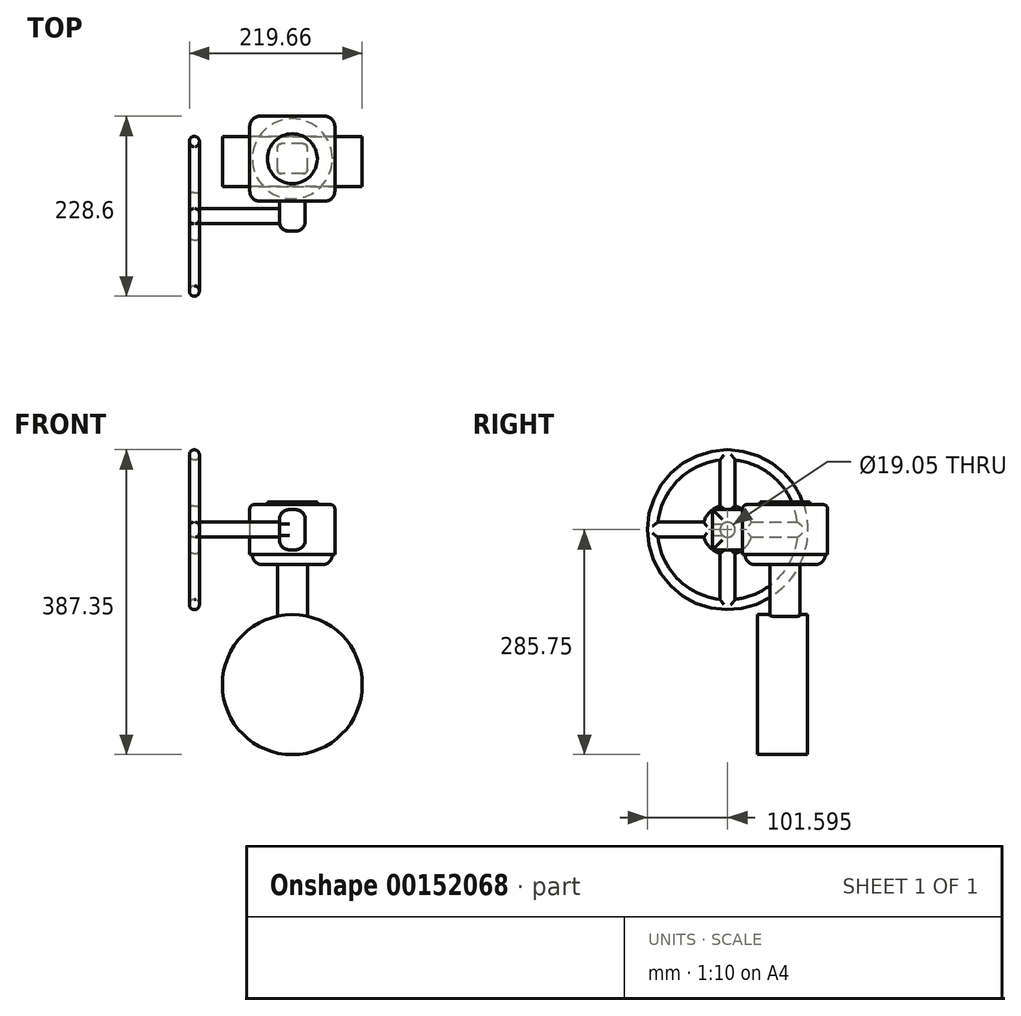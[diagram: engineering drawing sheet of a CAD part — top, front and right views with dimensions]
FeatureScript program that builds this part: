
annotation { "Feature Type Name" : "Feature", "Feature Type Description" : "" }
export const myFeature = defineFeature(function(context is Context, id is Id, definition is map)
    precondition{}
    {
        {
            var Q0;
            Q0=qCreatedBy(makeId("Front.planeOp"),FACE);
            var sketch = newSketch(context, id + "F0", { "sketchPlane" : qUnion([Q0])});
            skCircle(sketch, "E0", {"center": v(0, 0) * mm, "radius": 88.9 * mm});
            skSolve(sketch);
        }
        {
            var Q0;
            Q0=qSketchRegion(id+"F0",true);
            extrude(context, id + "F1", {"entities" : qUnion([Q0]), "depth" : 63.5 * mm});
        }
        {
            var Q0;
            Q0=qCreatedBy(makeId("Top.planeOp"),FACE);
            var sketch = newSketch(context, id + "F2", { "sketchPlane" : qUnion([Q0])});
            skLineSegment(sketch, "E1.bottom", {"start": v(19.05, -9.05) * mm, "end": v(-19.05, -9.05) * mm});
            skLineSegment(sketch, "E1.top", {"start": v(19.05, -47.15) * mm, "end": v(-19.05, -47.15) * mm});
            skLineSegment(sketch, "E1.left", {"start": v(19.05, -9.05) * mm, "end": v(19.05, -47.15) * mm});
            skLineSegment(sketch, "E1.right", {"start": v(-19.05, -9.05) * mm, "end": v(-19.05, -47.15) * mm});
            skPoint(sketch, "E1.middle", {"position": v(0, -28.1) * mm});
            skSolve(sketch);
        }
        {
            var Q0;
            Q0=qSketchRegion(id+"F2",true);
            extrude(context, id + "F3", {"entities" : qUnion([Q0]), "operationType" : NewBodyOperationType.ADD, "depth" : 152.4 * mm});
        }
        {
            var Q0;
            Q0=makeQuery(id+"F3.opExtrude","CAP_FACE",FACE,{"disambiguationData":[OSD([sQuery(id+"F2.wireOp",EDGE,"E1.bottom"),sQuery(id+"F2.wireOp",EDGE,"E1.top"),sQuery(id+"F2.wireOp",EDGE,"E1.left"),sQuery(id+"F2.wireOp",EDGE,"E1.right")])],"isStart":false});
            var sketch = newSketch(context, id + "F4", { "sketchPlane" : qUnion([Q0])});
            skCircle(sketch, "E2", {"center": v(0, -28.1) * mm, "radius": 50.8 * mm});
            skPoint(sketch, "E2.centerSnap0", {"position": v(19.05, -28.1) * mm});
            skSolve(sketch);
        }
        {
            var Q0;
            Q0=qSketchRegion(id+"F4",true);
            extrude(context, id + "F5", {"entities" : qUnion([Q0]), "operationType" : NewBodyOperationType.ADD, "depth" : 12.7 * mm});
        }
        {
            var Q0;
            Q0=makeQuery(id+"F5.opExtrude","CAP_FACE",FACE,{"disambiguationData":[OSD([sQuery(id+"F4.wireOp",EDGE,"E2")])],"isStart":false});
            var sketch = newSketch(context, id + "F6", { "sketchPlane" : qUnion([Q0])});
            skCircle(sketch, "E3", {"center": v(0, -28.1) * mm, "radius": 9.5 * mm});
            skSolve(sketch);
        }
        {
            var Q0;
            Q0=makeQuery(id+"F3.opExtrude","SWEPT_EDGE",EDGE,{"disambiguationData":[OSD([sQuery(id+"F2.wireOp",EDGE,"E1.top"),sQuery(id+"F2.wireOp",EDGE,"E1.right")])]});
            var Q1;
            Q1=makeQuery(id+"F3.opExtrude","SWEPT_EDGE",EDGE,{"disambiguationData":[OSD([sQuery(id+"F2.wireOp",EDGE,"E1.top"),sQuery(id+"F2.wireOp",EDGE,"E1.left")])]});
            var Q2;
            Q2=makeQuery(id+"F3.opExtrude","SWEPT_EDGE",EDGE,{"disambiguationData":[OSD([sQuery(id+"F2.wireOp",EDGE,"E1.bottom"),sQuery(id+"F2.wireOp",EDGE,"E1.left")])]});
            var Q3;
            Q3=makeQuery(id+"F3.opExtrude","SWEPT_EDGE",EDGE,{"disambiguationData":[OSD([sQuery(id+"F2.wireOp",EDGE,"E1.bottom"),sQuery(id+"F2.wireOp",EDGE,"E1.right")])]});
            fillet(context, id + "F7", {"entities" : qUnion([Q0, Q1, Q2, Q3]), "radius" : 5.08 * mm, "tangentPropagation" : true, "allowEdgeOverflow" : false});
        }
        {
            var Q0;
            Q0=sQuery(id+"F6.wireOp",EDGE,"E3");
            extrude(context, id + "F8", {"bodyType" : ToolBodyType.SURFACE, "surfaceEntities" : qUnion([Q0]), "depth" : 31.75 * mm});
        }
        {
            var Q0;
            Q0=makeQuery(id+"F5.opExtrude","CAP_FACE",FACE,{"disambiguationData":[OSD([sQuery(id+"F4.wireOp",EDGE,"E2")])],"isStart":false});
            var sketch = newSketch(context, id + "F9", { "sketchPlane" : qUnion([Q0])});
            skLineSegment(sketch, "E4.bottom", {"start": v(53.98, 25.88) * mm, "end": v(-53.98, 25.88) * mm});
            skLineSegment(sketch, "E4.top", {"start": v(53.97, -82.07) * mm, "end": v(-53.98, -82.07) * mm});
            skLineSegment(sketch, "E4.left", {"start": v(53.98, 25.88) * mm, "end": v(53.97, -82.07) * mm});
            skLineSegment(sketch, "E4.right", {"start": v(-53.97, 25.88) * mm, "end": v(-53.98, -82.07) * mm});
            skPoint(sketch, "E4.middle", {"position": v(0, -28.1) * mm});
            skSolve(sketch);
        }
        {
            var Q0;
            Q0 = qSketchRegion(id + "F9", true);
            extrude(context, id + "F10", {"entities" : qUnion([Q0]), "operationType" : NewBodyOperationType.ADD, "depth" : 63.5 * mm});
        }
        {
            var Q0;
            Q0=makeQuery(id+"F10.opExtrude","SWEPT_FACE",FACE,{"disambiguationData":[OSD([sQuery(id+"F9.wireOp",EDGE,"E4.top")])]});
            var sketch = newSketch(context, id + "F11", { "sketchPlane" : qUnion([Q0])});
            skLineSegment(sketch, "E5.bottom", {"start": v(16.46, 222.43) * mm, "end": v(-16.46, 222.43) * mm});
            skLineSegment(sketch, "E5.top", {"start": v(16.46, 171.27) * mm, "end": v(-16.46, 171.27) * mm});
            skLineSegment(sketch, "E5.left", {"start": v(16.46, 222.43) * mm, "end": v(16.46, 171.27) * mm});
            skLineSegment(sketch, "E5.right", {"start": v(-16.46, 222.43) * mm, "end": v(-16.46, 171.27) * mm});
            skPoint(sketch, "E5.middle", {"position": v(0, 196.85) * mm});
            skPoint(sketch, "E5.middle.positionSnap0", {"position": v(53.98, 196.85) * mm});
            skPoint(sketch, "E5.centerSnap0", {"position": v(53.98, 196.85) * mm});
            skSolve(sketch);
        }
        {
            var Q0;
            Q0 = qSketchRegion(id + "F11", true);
            extrude(context, id + "F12", {"entities" : qUnion([Q0]), "operationType" : NewBodyOperationType.ADD, "depth" : 38.1 * mm});
        }
        {
            var Q0;
            Q0=makeQuery(id+"F12.opExtrude","SWEPT_FACE",FACE,{"disambiguationData":[OSD([sQuery(id+"F11.wireOp",EDGE,"E5.right")])]});
            var sketch = newSketch(context, id + "F13", { "sketchPlane" : qUnion([Q0])});
            skCircle(sketch, "E6", {"center": v(101.12, 196.85) * mm, "radius": 9.53 * mm});
            skPoint(sketch, "E6.centerSnap0", {"position": v(101.12, 171.27) * mm});
            skPoint(sketch, "E6.centerSnap1", {"position": v(120.17, 196.85) * mm});
            skSolve(sketch);
        }
        {
            var Q0;
            Q0 = qSketchRegion(id + "F13", true);
            extrude(context, id + "F14", {"entities" : qUnion([Q0]), "operationType" : NewBodyOperationType.ADD, "depth" : 101.6 * mm});
        }
        {
            var Q0;
            Q0=makeQuery(id+"F14.opExtrude","CAP_FACE",FACE,{"disambiguationData":[OSD([sQuery(id+"F13.wireOp",EDGE,"E6")])],"isStart":false});
            var sketch = newSketch(context, id + "F15", { "sketchPlane" : qUnion([Q0])});
            skCircle(sketch, "E7", {"center": v(101.12, 196.85) * mm, "radius": 101.6 * mm});
            skCircle(sketch, "E8", {"center": v(101.12, 196.85) * mm, "radius": 31.75 * mm});
            skCircle(sketch, "E9", {"center": v(101.12, 196.85) * mm, "radius": 88.9 * mm});
            skLineSegment(sketch, "E10.bottom", {"start": v(189.51, 206.37) * mm, "end": v(131.41, 206.37) * mm});
            skLineSegment(sketch, "E10.top", {"start": v(189.51, 187.32) * mm, "end": v(131.41, 187.32) * mm});
            skPoint(sketch, "E10.middle", {"position": v(158.95, 196.85) * mm});
            skLineSegment(sketch, "E11.left", {"start": v(110.65, 166.56) * mm, "end": v(110.65, 108.46) * mm});
            skLineSegment(sketch, "E11.right", {"start": v(91.6, 166.56) * mm, "end": v(91.6, 108.46) * mm});
            skPoint(sketch, "E11.middle", {"position": v(101.12, 139.25) * mm});
            skLineSegment(sketch, "E12.bottom", {"start": v(70.84, 206.38) * mm, "end": v(12.74, 206.38) * mm});
            skLineSegment(sketch, "E12.top", {"start": v(70.84, 187.32) * mm, "end": v(12.74, 187.32) * mm});
            skPoint(sketch, "E12.middle", {"position": v(45.52, 196.85) * mm});
            skLineSegment(sketch, "E13.left", {"start": v(110.65, 285.24) * mm, "end": v(110.65, 227.14) * mm});
            skLineSegment(sketch, "E13.right", {"start": v(91.6, 285.24) * mm, "end": v(91.6, 227.14) * mm});
            skPoint(sketch, "E13.middle", {"position": v(101.12, 255.79) * mm});
            skPoint(sketch, "E14.orphan", {"position": v(110.65, 102.77) * mm});
            skPoint(sketch, "E15.orphan", {"position": v(91.6, 102.77) * mm});
            skPoint(sketch, "E16.orphan", {"position": v(110.65, 175.72) * mm});
            skPoint(sketch, "E17.orphan", {"position": v(91.6, 175.72) * mm});
            skPoint(sketch, "E18.orphan", {"position": v(127.2, 206.37) * mm});
            skPoint(sketch, "E19.orphan", {"position": v(127.2, 187.32) * mm});
            skPoint(sketch, "E20.orphan", {"position": v(190.7, 187.32) * mm});
            skPoint(sketch, "E21.orphan", {"position": v(190.7, 206.37) * mm});
            skPoint(sketch, "E22.orphan", {"position": v(91.6, 217.69) * mm});
            skPoint(sketch, "E13.top.start.orphan", {"position": v(110.65, 217.69) * mm});
            skPoint(sketch, "E23.orphan", {"position": v(91.6, 293.89) * mm});
            skPoint(sketch, "E13.bottom.start.orphan", {"position": v(110.65, 293.89) * mm});
            skPoint(sketch, "E24.orphan", {"position": v(83.62, 206.38) * mm});
            skPoint(sketch, "E12.left.end.orphan", {"position": v(83.62, 187.32) * mm});
            skPoint(sketch, "E25.orphan", {"position": v(7.42, 187.32) * mm});
            skPoint(sketch, "E12.right.start.orphan", {"position": v(7.42, 206.38) * mm});
            skCircle(sketch, "E26", {"center": v(101.12, 196.85) * mm, "radius": 9.52 * mm});
            skSolve(sketch);
        }
        {
            var Q0;
            Q0 = qSketchRegion(id + "F15", true);
            var Q1;
            {var subQ0=sQuery(id+"F15.wireOp",EDGE,"E13.left");Q1=makeQuery(id+"F15.imprint","IMPRINT",FACE,{"disambiguationData":[TD([[makeQuery(id+"F15.imprint","IMPRINT",EDGE,{"derivedFrom":subQ0}),-1.0]])]});}
            var Q2;
            {var subQ0=sQuery(id+"F15.wireOp",EDGE,"E12.bottom");Q2=makeQuery(id+"F15.imprint","IMPRINT",FACE,{"disambiguationData":[TD([[makeQuery(id+"F15.imprint","IMPRINT",EDGE,{"derivedFrom":subQ0}),1.0]])]});}
            var Q3;
            {var subQ0=sQuery(id+"F15.wireOp",EDGE,"E10.bottom");Q3=makeQuery(id+"F15.imprint","IMPRINT",FACE,{"disambiguationData":[TD([[makeQuery(id+"F15.imprint","IMPRINT",EDGE,{"derivedFrom":subQ0}),1.0]])]});}
            var Q4;
            {var subQ0=sQuery(id+"F15.wireOp",EDGE,"E11.left");Q4=makeQuery(id+"F15.imprint","IMPRINT",FACE,{"disambiguationData":[TD([[makeQuery(id+"F15.imprint","IMPRINT",EDGE,{"derivedFrom":subQ0}),-1.0]])]});}
            var Q5;
            Q5=makeQuery(id+"F15.imprint","IMPRINT",FACE,{"disambiguationData":[TD([[makeQuery(id+"F15.imprint","IMPRINT",EDGE,{"derivedFrom":sQuery(id+"F15.wireOp",EDGE,"E26")}),-1.0]])]});
            extrude(context, id + "F16", {"entities" : qUnion([Q0, Q1, Q2, Q3, Q4, Q5]), "depth" : 12.7 * mm});
        }
        {
            var Q0;
            Q0=makeQuery(id+"F16.opExtrude","CAP_EDGE",EDGE,{"disambiguationData":[OSD([sQuery(id+"F15.wireOp",EDGE,"E7")])],"isStart":false});
            var Q1;
            Q1=makeQuery(id+"F16.opExtrude","CAP_EDGE",EDGE,{"disambiguationData":[OSD([sQuery(id+"F15.wireOp",EDGE,"E7")])],"isStart":true});
            var Q2;
            {var subQ0=sQuery(id+"F15.wireOp",EDGE,"E9");Q2=makeQuery(id+"F16.opExtrude","CAP_EDGE",EDGE,{"disambiguationData":[OSD([subQ0]),TDD([makeQuery(id+"F15.imprint","IMPRINT",EDGE,{"disambiguationData":[TD([[makeQuery(id+"F15.imprint","INTERSECT",VERTEX,{"derivedFrom":[subQ0,sQuery(id+"F15.wireOp",EDGE,"E10.top")]}),1.0]])],"derivedFrom":subQ0})])],"isStart":false});}
            var Q3;
            {var subQ0=sQuery(id+"F15.wireOp",EDGE,"E9");Q3=makeQuery(id+"F16.opExtrude","CAP_EDGE",EDGE,{"disambiguationData":[OSD([subQ0]),TDD([makeQuery(id+"F15.imprint","IMPRINT",EDGE,{"disambiguationData":[TD([[makeQuery(id+"F15.imprint","INTERSECT",VERTEX,{"derivedFrom":[subQ0,sQuery(id+"F15.wireOp",EDGE,"E10.bottom")]}),-1.0]])],"derivedFrom":subQ0})])],"isStart":false});}
            var Q4;
            {var subQ0=sQuery(id+"F15.wireOp",EDGE,"E9");Q4=makeQuery(id+"F16.opExtrude","CAP_EDGE",EDGE,{"disambiguationData":[OSD([subQ0]),TDD([makeQuery(id+"F15.imprint","IMPRINT",EDGE,{"disambiguationData":[TD([[makeQuery(id+"F15.imprint","INTERSECT",VERTEX,{"derivedFrom":[subQ0,sQuery(id+"F15.wireOp",EDGE,"E12.bottom")]}),1.0]])],"derivedFrom":subQ0})])],"isStart":false});}
            var Q5;
            {var subQ0=sQuery(id+"F15.wireOp",EDGE,"E9");Q5=makeQuery(id+"F16.opExtrude","CAP_EDGE",EDGE,{"disambiguationData":[OSD([subQ0]),TDD([makeQuery(id+"F15.imprint","IMPRINT",EDGE,{"disambiguationData":[TD([[makeQuery(id+"F15.imprint","INTERSECT",VERTEX,{"derivedFrom":[subQ0,sQuery(id+"F15.wireOp",EDGE,"E11.right")]}),1.0]])],"derivedFrom":subQ0})])],"isStart":false});}
            var Q6;
            {var subQ0=sQuery(id+"F15.wireOp",EDGE,"E9");Q6=makeQuery(id+"F16.opExtrude","CAP_EDGE",EDGE,{"disambiguationData":[OSD([subQ0]),TDD([makeQuery(id+"F15.imprint","IMPRINT",EDGE,{"disambiguationData":[TD([[makeQuery(id+"F15.imprint","INTERSECT",VERTEX,{"derivedFrom":[subQ0,sQuery(id+"F15.wireOp",EDGE,"E10.bottom")]}),-1.0]])],"derivedFrom":subQ0})])],"isStart":true});}
            var Q7;
            {var subQ0=sQuery(id+"F15.wireOp",EDGE,"E9");Q7=makeQuery(id+"F16.opExtrude","CAP_EDGE",EDGE,{"disambiguationData":[OSD([subQ0]),TDD([makeQuery(id+"F15.imprint","IMPRINT",EDGE,{"disambiguationData":[TD([[makeQuery(id+"F15.imprint","INTERSECT",VERTEX,{"derivedFrom":[subQ0,sQuery(id+"F15.wireOp",EDGE,"E10.top")]}),1.0]])],"derivedFrom":subQ0})])],"isStart":true});}
            var Q8;
            {var subQ0=sQuery(id+"F15.wireOp",EDGE,"E9");Q8=makeQuery(id+"F16.opExtrude","CAP_EDGE",EDGE,{"disambiguationData":[OSD([subQ0]),TDD([makeQuery(id+"F15.imprint","IMPRINT",EDGE,{"disambiguationData":[TD([[makeQuery(id+"F15.imprint","INTERSECT",VERTEX,{"derivedFrom":[subQ0,sQuery(id+"F15.wireOp",EDGE,"E11.right")]}),1.0]])],"derivedFrom":subQ0})])],"isStart":true});}
            var Q9;
            {var subQ0=sQuery(id+"F15.wireOp",EDGE,"E9");Q9=makeQuery(id+"F16.opExtrude","CAP_EDGE",EDGE,{"disambiguationData":[OSD([subQ0]),TDD([makeQuery(id+"F15.imprint","IMPRINT",EDGE,{"disambiguationData":[TD([[makeQuery(id+"F15.imprint","INTERSECT",VERTEX,{"derivedFrom":[subQ0,sQuery(id+"F15.wireOp",EDGE,"E12.bottom")]}),1.0]])],"derivedFrom":subQ0})])],"isStart":true});}
            fillet(context, id + "F17", {"entities" : qUnion([Q0, Q1, Q2, Q3, Q4, Q5, Q6, Q7, Q8, Q9]), "radius" : 6.35 * mm, "tangentPropagation" : true, "allowEdgeOverflow" : false});
        }
        {
            var Q0;
            {var subQ0=sQuery(id+"F15.wireOp",EDGE,"E8");Q0=makeQuery(id+"F16.opExtrude","CAP_EDGE",EDGE,{"disambiguationData":[OSD([subQ0]),TDD([makeQuery(id+"F15.imprint","IMPRINT",EDGE,{"disambiguationData":[TD([[makeQuery(id+"F15.imprint","INTERSECT",VERTEX,{"derivedFrom":[subQ0,sQuery(id+"F15.wireOp",EDGE,"E10.top")]}),1.0]])],"derivedFrom":subQ0})])],"isStart":false});}
            var Q1;
            {var subQ0=sQuery(id+"F15.wireOp",EDGE,"E8");Q1=makeQuery(id+"F16.opExtrude","CAP_EDGE",EDGE,{"disambiguationData":[OSD([subQ0]),TDD([makeQuery(id+"F15.imprint","IMPRINT",EDGE,{"disambiguationData":[TD([[makeQuery(id+"F15.imprint","INTERSECT",VERTEX,{"derivedFrom":[subQ0,sQuery(id+"F15.wireOp",EDGE,"E11.right")]}),1.0]])],"derivedFrom":subQ0})])],"isStart":false});}
            var Q2;
            {var subQ0=sQuery(id+"F15.wireOp",EDGE,"E8");Q2=makeQuery(id+"F16.opExtrude","CAP_EDGE",EDGE,{"disambiguationData":[OSD([subQ0]),TDD([makeQuery(id+"F15.imprint","IMPRINT",EDGE,{"disambiguationData":[TD([[makeQuery(id+"F15.imprint","INTERSECT",VERTEX,{"derivedFrom":[subQ0,sQuery(id+"F15.wireOp",EDGE,"E12.bottom")]}),1.0]])],"derivedFrom":subQ0})])],"isStart":false});}
            var Q3;
            {var subQ0=sQuery(id+"F15.wireOp",EDGE,"E8");Q3=makeQuery(id+"F16.opExtrude","CAP_EDGE",EDGE,{"disambiguationData":[OSD([subQ0]),TDD([makeQuery(id+"F15.imprint","IMPRINT",EDGE,{"disambiguationData":[TD([[makeQuery(id+"F15.imprint","INTERSECT",VERTEX,{"derivedFrom":[subQ0,sQuery(id+"F15.wireOp",EDGE,"E10.bottom")]}),-1.0]])],"derivedFrom":subQ0})])],"isStart":false});}
            var Q4;
            Q4=makeQuery(id+"F16.opExtrude","CAP_EDGE",EDGE,{"disambiguationData":[OSD([sQuery(id+"F15.wireOp",EDGE,"E10.top")])],"isStart":false});
            var Q5;
            Q5=makeQuery(id+"F16.opExtrude","CAP_EDGE",EDGE,{"disambiguationData":[OSD([sQuery(id+"F15.wireOp",EDGE,"E11.left")])],"isStart":false});
            var Q6;
            Q6=makeQuery(id+"F16.opExtrude","CAP_EDGE",EDGE,{"disambiguationData":[OSD([sQuery(id+"F15.wireOp",EDGE,"E11.right")])],"isStart":false});
            var Q7;
            Q7=makeQuery(id+"F16.opExtrude","CAP_EDGE",EDGE,{"disambiguationData":[OSD([sQuery(id+"F15.wireOp",EDGE,"E12.top")])],"isStart":false});
            var Q8;
            Q8=makeQuery(id+"F16.opExtrude","CAP_EDGE",EDGE,{"disambiguationData":[OSD([sQuery(id+"F15.wireOp",EDGE,"E12.bottom")])],"isStart":false});
            var Q9;
            Q9=makeQuery(id+"F16.opExtrude","CAP_EDGE",EDGE,{"disambiguationData":[OSD([sQuery(id+"F15.wireOp",EDGE,"E13.right")])],"isStart":false});
            var Q10;
            Q10=makeQuery(id+"F16.opExtrude","CAP_EDGE",EDGE,{"disambiguationData":[OSD([sQuery(id+"F15.wireOp",EDGE,"E13.left")])],"isStart":false});
            var Q11;
            Q11=makeQuery(id+"F16.opExtrude","CAP_EDGE",EDGE,{"disambiguationData":[OSD([sQuery(id+"F15.wireOp",EDGE,"E10.bottom")])],"isStart":false});
            var Q12;
            Q12=makeQuery(id+"F16.opExtrude","CAP_EDGE",EDGE,{"disambiguationData":[OSD([sQuery(id+"F15.wireOp",EDGE,"E11.right")])],"isStart":true});
            var Q13;
            Q13=makeQuery(id+"F16.opExtrude","CAP_EDGE",EDGE,{"disambiguationData":[OSD([sQuery(id+"F15.wireOp",EDGE,"E11.left")])],"isStart":true});
            var Q14;
            Q14=makeQuery(id+"F16.opExtrude","CAP_EDGE",EDGE,{"disambiguationData":[OSD([sQuery(id+"F15.wireOp",EDGE,"E10.top")])],"isStart":true});
            var Q15;
            Q15=makeQuery(id+"F16.opExtrude","CAP_EDGE",EDGE,{"disambiguationData":[OSD([sQuery(id+"F15.wireOp",EDGE,"E10.bottom")])],"isStart":true});
            var Q16;
            Q16=makeQuery(id+"F16.opExtrude","CAP_EDGE",EDGE,{"disambiguationData":[OSD([sQuery(id+"F15.wireOp",EDGE,"E13.left")])],"isStart":true});
            var Q17;
            Q17=makeQuery(id+"F16.opExtrude","CAP_EDGE",EDGE,{"disambiguationData":[OSD([sQuery(id+"F15.wireOp",EDGE,"E13.right")])],"isStart":true});
            var Q18;
            Q18=makeQuery(id+"F16.opExtrude","CAP_EDGE",EDGE,{"disambiguationData":[OSD([sQuery(id+"F15.wireOp",EDGE,"E12.bottom")])],"isStart":true});
            var Q19;
            Q19=makeQuery(id+"F16.opExtrude","CAP_EDGE",EDGE,{"disambiguationData":[OSD([sQuery(id+"F15.wireOp",EDGE,"E12.top")])],"isStart":true});
            var Q20;
            {var subQ0=sQuery(id+"F15.wireOp",EDGE,"E8");Q20=makeQuery(id+"F16.opExtrude","CAP_EDGE",EDGE,{"disambiguationData":[OSD([subQ0]),TDD([makeQuery(id+"F15.imprint","IMPRINT",EDGE,{"disambiguationData":[TD([[makeQuery(id+"F15.imprint","INTERSECT",VERTEX,{"derivedFrom":[subQ0,sQuery(id+"F15.wireOp",EDGE,"E11.right")]}),1.0]])],"derivedFrom":subQ0})])],"isStart":true});}
            var Q21;
            {var subQ0=sQuery(id+"F15.wireOp",EDGE,"E8");Q21=makeQuery(id+"F16.opExtrude","CAP_EDGE",EDGE,{"disambiguationData":[OSD([subQ0]),TDD([makeQuery(id+"F15.imprint","IMPRINT",EDGE,{"disambiguationData":[TD([[makeQuery(id+"F15.imprint","INTERSECT",VERTEX,{"derivedFrom":[subQ0,sQuery(id+"F15.wireOp",EDGE,"E10.top")]}),1.0]])],"derivedFrom":subQ0})])],"isStart":true});}
            var Q22;
            {var subQ0=sQuery(id+"F15.wireOp",EDGE,"E8");Q22=makeQuery(id+"F16.opExtrude","CAP_EDGE",EDGE,{"disambiguationData":[OSD([subQ0]),TDD([makeQuery(id+"F15.imprint","IMPRINT",EDGE,{"disambiguationData":[TD([[makeQuery(id+"F15.imprint","INTERSECT",VERTEX,{"derivedFrom":[subQ0,sQuery(id+"F15.wireOp",EDGE,"E10.bottom")]}),-1.0]])],"derivedFrom":subQ0})])],"isStart":true});}
            var Q23;
            {var subQ0=sQuery(id+"F15.wireOp",EDGE,"E8");Q23=makeQuery(id+"F16.opExtrude","CAP_EDGE",EDGE,{"disambiguationData":[OSD([subQ0]),TDD([makeQuery(id+"F15.imprint","IMPRINT",EDGE,{"disambiguationData":[TD([[makeQuery(id+"F15.imprint","INTERSECT",VERTEX,{"derivedFrom":[subQ0,sQuery(id+"F15.wireOp",EDGE,"E12.bottom")]}),1.0]])],"derivedFrom":subQ0})])],"isStart":true});}
            fillet(context, id + "F18", {"entities" : qUnion([Q0, Q1, Q2, Q3, Q4, Q5, Q6, Q7, Q8, Q9, Q10, Q11, Q12, Q13, Q14, Q15, Q16, Q17, Q18, Q19, Q20, Q21, Q22, Q23]), "radius" : 5.08 * mm, "tangentPropagation" : true, "allowEdgeOverflow" : false});
        }
        {
            var Q0;
            Q0=makeQuery(id+"F10.opExtrude","SWEPT_EDGE",EDGE,{"disambiguationData":[OSD([sQuery(id+"F9.wireOp",EDGE,"E4.bottom"),sQuery(id+"F9.wireOp",EDGE,"E4.right")])]});
            var Q1;
            Q1=makeQuery(id+"F10.opExtrude","SWEPT_EDGE",EDGE,{"disambiguationData":[OSD([sQuery(id+"F9.wireOp",EDGE,"E4.top"),sQuery(id+"F9.wireOp",EDGE,"E4.right")])]});
            var Q2;
            Q2=makeQuery(id+"F10.opExtrude","SWEPT_EDGE",EDGE,{"disambiguationData":[OSD([sQuery(id+"F9.wireOp",EDGE,"E4.bottom"),sQuery(id+"F9.wireOp",EDGE,"E4.left")])]});
            var Q3;
            Q3=makeQuery(id+"F10.opExtrude","SWEPT_EDGE",EDGE,{"disambiguationData":[OSD([sQuery(id+"F9.wireOp",EDGE,"E4.top"),sQuery(id+"F9.wireOp",EDGE,"E4.left")])]});
            var Q4;
            Q4=makeQuery(id+"F12.opExtrude","SWEPT_EDGE",EDGE,{"disambiguationData":[OSD([sQuery(id+"F11.wireOp",EDGE,"E5.bottom"),sQuery(id+"F11.wireOp",EDGE,"E5.left")])]});
            var Q5;
            Q5=makeQuery(id+"F12.opExtrude","CAP_EDGE",EDGE,{"disambiguationData":[OSD([sQuery(id+"F11.wireOp",EDGE,"E5.left")])],"isStart":false});
            var Q6;
            Q6=makeQuery(id+"F12.opExtrude","SWEPT_EDGE",EDGE,{"disambiguationData":[OSD([sQuery(id+"F11.wireOp",EDGE,"E5.top"),sQuery(id+"F11.wireOp",EDGE,"E5.left")])]});
            var Q7;
            Q7=makeQuery(id+"F12.opExtrude","CAP_EDGE",EDGE,{"disambiguationData":[OSD([sQuery(id+"F11.wireOp",EDGE,"E5.right")])],"isStart":false});
            var Q8;
            Q8=makeQuery(id+"F12.opExtrude","SWEPT_EDGE",EDGE,{"disambiguationData":[OSD([sQuery(id+"F11.wireOp",EDGE,"E5.bottom"),sQuery(id+"F11.wireOp",EDGE,"E5.right")])]});
            var Q9;
            Q9=makeQuery(id+"F12.opExtrude","SWEPT_EDGE",EDGE,{"disambiguationData":[OSD([sQuery(id+"F11.wireOp",EDGE,"E5.top"),sQuery(id+"F11.wireOp",EDGE,"E5.right")])]});
            var Q10;
            Q10=makeQuery(id+"F5.opExtrude","CAP_EDGE",EDGE,{"disambiguationData":[OSD([sQuery(id+"F4.wireOp",EDGE,"E2")])],"isStart":true});
            fillet(context, id + "F19", {"entities" : qUnion([Q0, Q1, Q2, Q3, Q4, Q5, Q6, Q7, Q8, Q9, Q10]), "radius" : 12.7 * mm, "tangentPropagation" : true, "allowEdgeOverflow" : false});
        }
        {
            var Q0;
            Q0=makeQuery(id+"F10.opExtrude","CAP_EDGE",EDGE,{"disambiguationData":[OSD([sQuery(id+"F9.wireOp",EDGE,"E4.top")])],"isStart":false});
            fillet(context, id + "F20", {"entities" : qUnion([Q0]), "radius" : 5.08 * mm, "tangentPropagation" : true, "allowEdgeOverflow" : false});
        }
        {
            var Q0;
            Q0=makeQuery(id+"F10.opExtrude","CAP_FACE",FACE,{"disambiguationData":[OSD([sQuery(id+"F9.wireOp",EDGE,"E4.bottom"),sQuery(id+"F9.wireOp",EDGE,"E4.top"),sQuery(id+"F9.wireOp",EDGE,"E4.left"),sQuery(id+"F9.wireOp",EDGE,"E4.right")])],"isStart":false});
            var sketch = newSketch(context, id + "F21", { "sketchPlane" : qUnion([Q0])});
            skCircle(sketch, "E27", {"center": v(0, -28.1) * mm, "radius": 31.75 * mm});
            skPoint(sketch, "E27.centerSnap0", {"position": v(-48.9, -28.1) * mm});
            skSolve(sketch);
        }
        {
            var Q0;
            Q0 = qSketchRegion(id + "F21", true);
            extrude(context, id + "F22", {"entities" : qUnion([Q0]), "operationType" : NewBodyOperationType.ADD, "depth" : 3.17 * mm});
        }
    });
